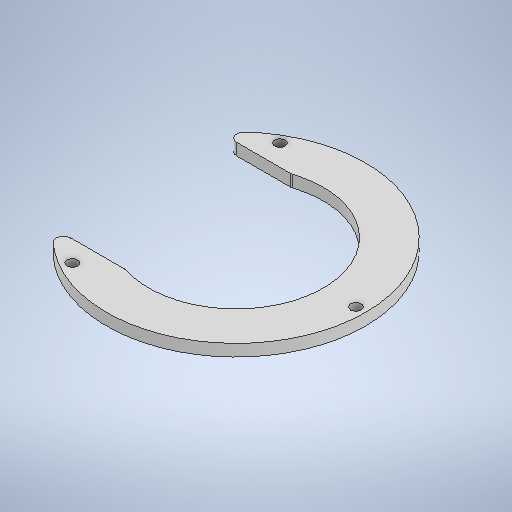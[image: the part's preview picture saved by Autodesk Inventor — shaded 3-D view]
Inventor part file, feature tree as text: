
AUTODESK INVENTOR PART (.ipt)
format: ipt  version: 2025.2 (Build 292293000, 293)  size: 285,696 bytes
history: native  units: in
note: dims shown in document units (in); Inventor stores cm internally (conversion verified against a paired STEP export)
features: extrude x2, sketch x2, fillet x1
ambient origin geometry x8: Origin, YZ Plane, XZ Plane, XY Plane, X Axis, Y Axis, Z Axis, Center Point
bodies: Solid1 (feature_tree)
feature tree (5):
  extrude  "Extrusion1"  Depth=6.378in
  fillet  "Fillet1"  Radius=6.8898in
  extrude  "Extrusion2"  Depth=4.4094in
  sketch  "Sketch1"  dims[d0=4.6457in d1=6.378in d2=6.8898in]
  sketch  "Sketch2"  dims[d5=0.315in d6=0.0in d7=4.4094in d9=3.1496in d10=0.3937in d11=0.1969in d12=0.1969in d13=0.3937in d14=0.0in]
